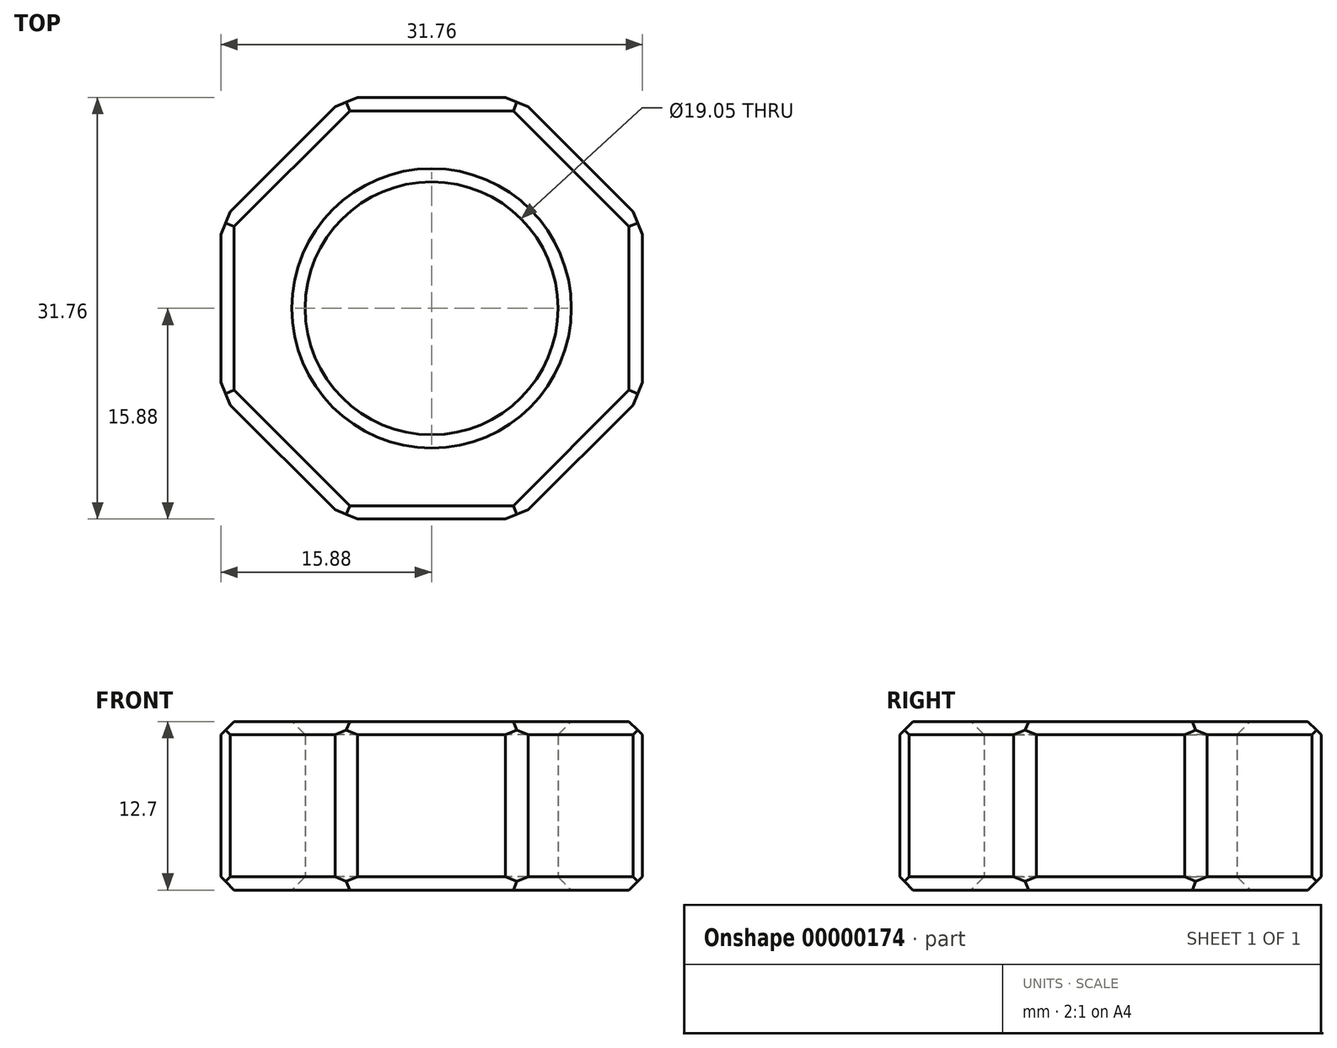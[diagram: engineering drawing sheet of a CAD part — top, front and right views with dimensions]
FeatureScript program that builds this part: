
annotation { "Feature Type Name" : "Feature", "Feature Type Description" : "" }
export const myFeature = defineFeature(function(context is Context, id is Id, definition is map)
    precondition{}
    {
        {
            var Q0;
            Q0=qCreatedBy(makeId("Top.planeOp"),FACE);
            var sketch = newSketch(context, id + "F0", { "sketchPlane" : qUnion([Q0])});
            skLineSegment(sketch, "E0", {"start": v(-15.88, 6.58) * mm, "end": v(-6.58, 15.88) * mm});
            skLineSegment(sketch, "E1", {"start": v(-6.58, 15.88) * mm, "end": v(6.58, 15.88) * mm});
            skLineSegment(sketch, "E2", {"start": v(6.58, 15.88) * mm, "end": v(15.88, 6.58) * mm});
            skLineSegment(sketch, "E3", {"start": v(15.88, 6.58) * mm, "end": v(15.88, -6.58) * mm});
            skLineSegment(sketch, "E4", {"start": v(15.88, -6.58) * mm, "end": v(6.58, -15.88) * mm});
            skLineSegment(sketch, "E5", {"start": v(6.58, -15.88) * mm, "end": v(-6.58, -15.88) * mm});
            skLineSegment(sketch, "E6", {"start": v(-6.58, -15.88) * mm, "end": v(-15.88, -6.58) * mm});
            skLineSegment(sketch, "E7", {"start": v(-15.88, -6.58) * mm, "end": v(-15.88, 6.58) * mm});
            skLineSegment(sketch, "E8", {"start": v(0, -15.88) * mm, "end": v(0, 15.88) * mm, "construction": true});
            skLineSegment(sketch, "E9", {"start": v(-15.88, 0) * mm, "end": v(15.88, 0) * mm, "construction": true});
            skCircle(sketch, "E10", {"center": v(0, 0) * mm, "radius": 9.53 * mm});
            skSolve(sketch);
        }
        {
            var Q0;
            Q0=makeQuery(id+"F0.imprint","IMPRINT",FACE,{"disambiguationData":[TD([[makeQuery(id+"F0.imprint","IMPRINT",EDGE,{"derivedFrom":sQuery(id+"F0.wireOp",EDGE,"E0")}),-1.0]])]});
            extrude(context, id + "F1", {"entities" : qUnion([Q0]), "depth" : 12.7 * mm});
        }
        {
            var Q0;
            Q0=makeQuery(id+"F1.opExtrude","CAP_FACE",FACE,{"disambiguationData":[OSD([sQuery(id+"F0.wireOp",EDGE,"E0"),sQuery(id+"F0.wireOp",EDGE,"E1"),sQuery(id+"F0.wireOp",EDGE,"E2"),sQuery(id+"F0.wireOp",EDGE,"E3"),sQuery(id+"F0.wireOp",EDGE,"E4"),sQuery(id+"F0.wireOp",EDGE,"E5"),sQuery(id+"F0.wireOp",EDGE,"E6"),sQuery(id+"F0.wireOp",EDGE,"E7"),sQuery(id+"F0.wireOp",EDGE,"E10")])],"isStart":true});
            var Q1;
            Q1=makeQuery(id+"F1.opExtrude","CAP_FACE",FACE,{"disambiguationData":[OSD([sQuery(id+"F0.wireOp",EDGE,"E0"),sQuery(id+"F0.wireOp",EDGE,"E1"),sQuery(id+"F0.wireOp",EDGE,"E2"),sQuery(id+"F0.wireOp",EDGE,"E3"),sQuery(id+"F0.wireOp",EDGE,"E4"),sQuery(id+"F0.wireOp",EDGE,"E5"),sQuery(id+"F0.wireOp",EDGE,"E6"),sQuery(id+"F0.wireOp",EDGE,"E7"),sQuery(id+"F0.wireOp",EDGE,"E10")])],"isStart":false});
            chamfer(context, id + "F2", {"entities" : qUnion([Q0, Q1]), "width" : 1 * mm, "tangentPropagation" : true});
        }
        {
            var Q0;
            Q0=makeQuery(id+"F1.opExtrude","SWEPT_EDGE",EDGE,{"disambiguationData":[OSD([sQuery(id+"F0.wireOp",EDGE,"E2"),sQuery(id+"F0.wireOp",EDGE,"E3")])]});
            var Q1;
            Q1=makeQuery(id+"F1.opExtrude","SWEPT_EDGE",EDGE,{"disambiguationData":[OSD([sQuery(id+"F0.wireOp",EDGE,"E1"),sQuery(id+"F0.wireOp",EDGE,"E2")])]});
            var Q2;
            Q2=makeQuery(id+"F1.opExtrude","SWEPT_EDGE",EDGE,{"disambiguationData":[OSD([sQuery(id+"F0.wireOp",EDGE,"E0"),sQuery(id+"F0.wireOp",EDGE,"E1")])]});
            var Q3;
            Q3=makeQuery(id+"F1.opExtrude","SWEPT_EDGE",EDGE,{"disambiguationData":[OSD([sQuery(id+"F0.wireOp",EDGE,"E0"),sQuery(id+"F0.wireOp",EDGE,"E7")])]});
            var Q4;
            Q4=makeQuery(id+"F1.opExtrude","SWEPT_EDGE",EDGE,{"disambiguationData":[OSD([sQuery(id+"F0.wireOp",EDGE,"E6"),sQuery(id+"F0.wireOp",EDGE,"E7")])]});
            var Q5;
            Q5=makeQuery(id+"F1.opExtrude","SWEPT_EDGE",EDGE,{"disambiguationData":[OSD([sQuery(id+"F0.wireOp",EDGE,"E5"),sQuery(id+"F0.wireOp",EDGE,"E6")])]});
            var Q6;
            Q6=makeQuery(id+"F1.opExtrude","SWEPT_EDGE",EDGE,{"disambiguationData":[OSD([sQuery(id+"F0.wireOp",EDGE,"E4"),sQuery(id+"F0.wireOp",EDGE,"E5")])]});
            var Q7;
            Q7=makeQuery(id+"F1.opExtrude","SWEPT_EDGE",EDGE,{"disambiguationData":[OSD([sQuery(id+"F0.wireOp",EDGE,"E3"),sQuery(id+"F0.wireOp",EDGE,"E4")])]});
            chamfer(context, id + "F3", {"entities" : qUnion([Q0, Q1, Q2, Q3, Q4, Q5, Q6, Q7]), "width" : 1 * mm, "tangentPropagation" : true});
        }
    });
